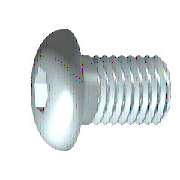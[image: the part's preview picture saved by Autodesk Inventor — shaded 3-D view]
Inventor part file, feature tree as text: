
AUTODESK INVENTOR PART (.ipt)
format: ipt  version: 2024 (Build 280153000, 153)  size: 195,072 bytes
history: native  units: mm (DEFAULTED — no unit token found)
features: extrude x1, plane x1, fillet x1
ambient origin geometry x7: Origin, YZ Plane, XY Plane, X Axis, Y Axis, Z Axis, Center Point
bodies: Solid1 (feature_tree), Body (feature_tree)
feature tree (3):
  extrude  "Slot"  Depth=10.5mm
  plane  "Work Plane1"
  fillet  "Fillet2"  Radius=0.306825mm
